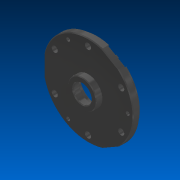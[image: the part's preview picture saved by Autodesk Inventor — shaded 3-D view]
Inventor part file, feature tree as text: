
AUTODESK INVENTOR PART (.ipt)
format: ipt  version: 2022.2 (Build 262287000, 287)  size: 1,312,256 bytes
history: native  units: in
note: dims shown in document units (in); Inventor stores cm internally (conversion verified against a paired STEP export)
features: chamfer x1
ambient origin geometry x8: Origin, YZ Plane, XZ Plane, XY Plane, X Axis, Y Axis, Z Axis, Center Point
bodies: Solid1 (feature_tree)
feature tree (1):
  chamfer  "Chamfer3"  [1 undecoded]
note: 1 required parameter value undecoded (feature->parameter linkage not recoverable at this tier; creation-order binding heuristic only, values carry confidence <= 0.55)
